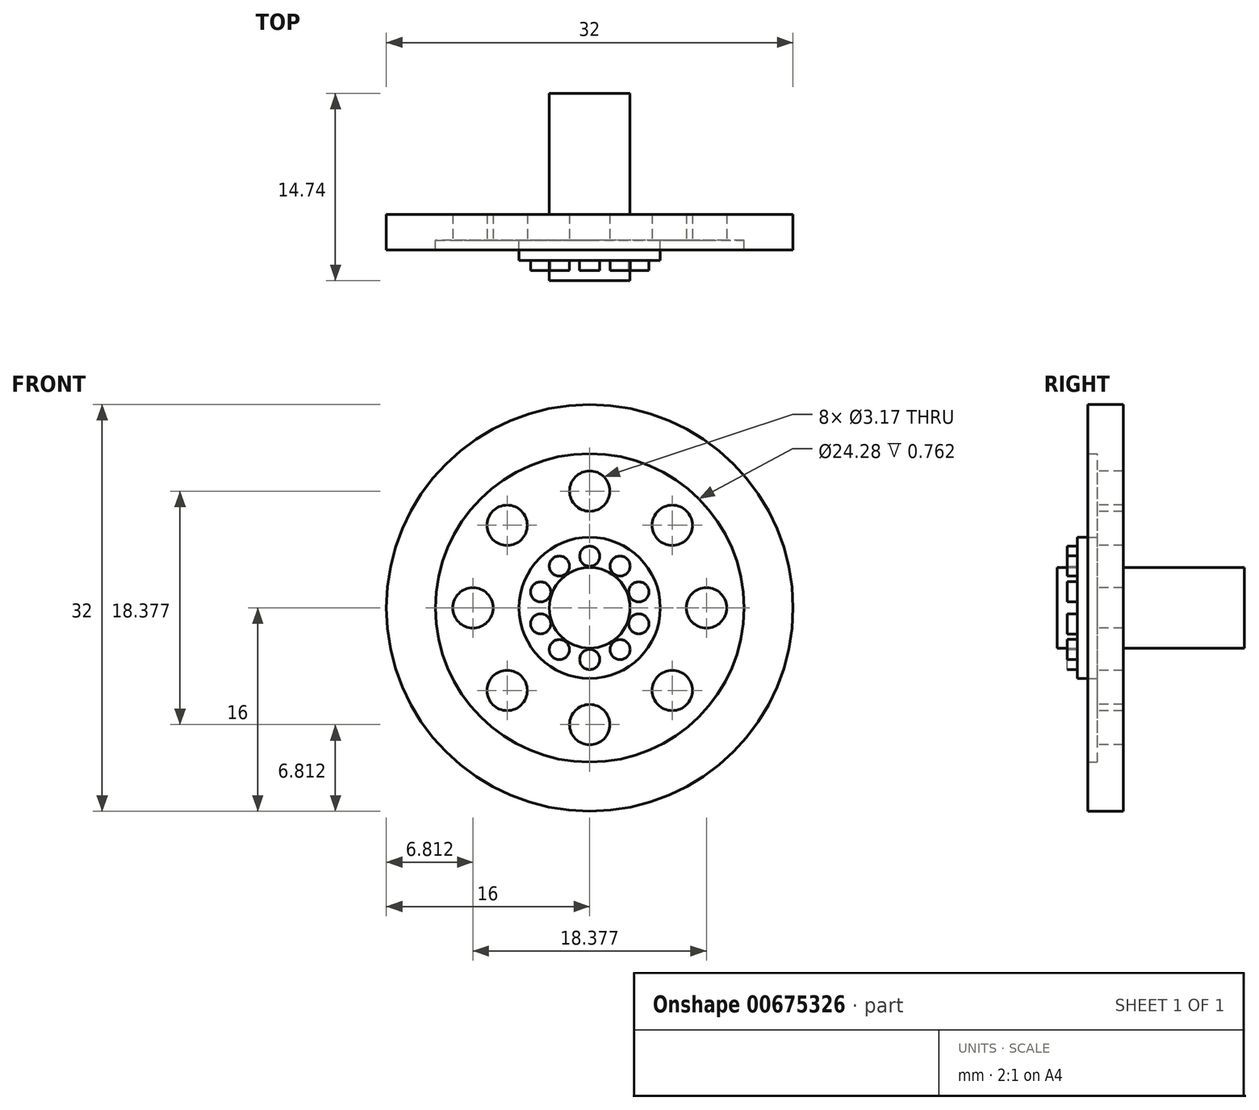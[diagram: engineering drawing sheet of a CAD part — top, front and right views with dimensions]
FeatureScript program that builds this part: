
annotation { "Feature Type Name" : "Feature", "Feature Type Description" : "" }
export const myFeature = defineFeature(function(context is Context, id is Id, definition is map)
    precondition{}
    {
        {
            var Q0;
            Q0=qCreatedBy(makeId("Front.planeOp"),FACE);
            var sketch = newSketch(context, id + "F0", { "sketchPlane" : qUnion([Q0])});
            skCircle(sketch, "E0", {"center": v(0, 0) * mm, "radius": 16 * mm});
            skSolve(sketch);
        }
        {
            var Q0;
            Q0 = qSketchRegion(id + "F0", true);
            extrude(context, id + "F1", {"entities" : qUnion([Q0]), "depth" : 2.03 * mm, "offsetDistance" : 25.4 * mm});
        }
        {
            var Q0;
            Q0=makeQuery(id+"F1.opExtrude","CAP_FACE",FACE,{"disambiguationData":[OSD([sQuery(id+"F0.wireOp",EDGE,"E0")])],"isStart":false});
            var sketch = newSketch(context, id + "F2", { "sketchPlane" : qUnion([Q0])});
            skCircle(sketch, "E1", {"center": v(0, 9.19) * mm, "radius": 1.59 * mm});
            skCircle(sketch, "E2.1.0", {"center": v(-6.5, 6.5) * mm, "radius": 1.59 * mm});
            skCircle(sketch, "E2.2.0", {"center": v(-9.19, 0) * mm, "radius": 1.59 * mm});
            skCircle(sketch, "E2.3.0", {"center": v(-6.5, -6.5) * mm, "radius": 1.59 * mm});
            skCircle(sketch, "E2.4.0", {"center": v(0, -9.19) * mm, "radius": 1.59 * mm});
            skCircle(sketch, "E2.5.0", {"center": v(6.5, -6.5) * mm, "radius": 1.59 * mm});
            skCircle(sketch, "E2.6.0", {"center": v(9.19, 0) * mm, "radius": 1.59 * mm});
            skCircle(sketch, "E2.7.0", {"center": v(6.5, 6.5) * mm, "radius": 1.59 * mm});
            skPoint(sketch, "E2.center", {"position": v(0, 0) * mm});
            skSolve(sketch);
        }
        {
            var Q0;
            Q0=makeQuery(id+"F2.imprint","IMPRINT",FACE,{"disambiguationData":[TD([[makeQuery(id+"F2.imprint","IMPRINT",EDGE,{"derivedFrom":sQuery(id+"F2.wireOp",EDGE,"E1")}),1.0]])]});
            var Q1;
            Q1=makeQuery(id+"F2.imprint","IMPRINT",FACE,{"disambiguationData":[TD([[makeQuery(id+"F2.imprint","IMPRINT",EDGE,{"derivedFrom":sQuery(id+"F2.wireOp",EDGE,"E2.7.0")}),1.0]])]});
            var Q2;
            Q2=makeQuery(id+"F2.imprint","IMPRINT",FACE,{"disambiguationData":[TD([[makeQuery(id+"F2.imprint","IMPRINT",EDGE,{"derivedFrom":sQuery(id+"F2.wireOp",EDGE,"E2.6.0")}),1.0]])]});
            var Q3;
            Q3=makeQuery(id+"F2.imprint","IMPRINT",FACE,{"disambiguationData":[TD([[makeQuery(id+"F2.imprint","IMPRINT",EDGE,{"derivedFrom":sQuery(id+"F2.wireOp",EDGE,"E2.5.0")}),1.0]])]});
            var Q4;
            Q4=makeQuery(id+"F2.imprint","IMPRINT",FACE,{"disambiguationData":[TD([[makeQuery(id+"F2.imprint","IMPRINT",EDGE,{"derivedFrom":sQuery(id+"F2.wireOp",EDGE,"E2.4.0")}),1.0]])]});
            var Q5;
            Q5=makeQuery(id+"F2.imprint","IMPRINT",FACE,{"disambiguationData":[TD([[makeQuery(id+"F2.imprint","IMPRINT",EDGE,{"derivedFrom":sQuery(id+"F2.wireOp",EDGE,"E2.3.0")}),1.0]])]});
            var Q6;
            Q6=makeQuery(id+"F2.imprint","IMPRINT",FACE,{"disambiguationData":[TD([[makeQuery(id+"F2.imprint","IMPRINT",EDGE,{"derivedFrom":sQuery(id+"F2.wireOp",EDGE,"E2.2.0")}),1.0]])]});
            var Q7;
            Q7=makeQuery(id+"F2.imprint","IMPRINT",FACE,{"disambiguationData":[TD([[makeQuery(id+"F2.imprint","IMPRINT",EDGE,{"derivedFrom":sQuery(id+"F2.wireOp",EDGE,"E2.1.0")}),1.0]])]});
            extrude(context, id + "F3", {"entities" : qUnion([Q0, Q1, Q2, Q3, Q4, Q5, Q6, Q7]), "operationType" : NewBodyOperationType.REMOVE, "oppositeDirection" : true, "depth" : 20.32 * mm, "offsetDistance" : 25.4 * mm});
        }
        {
            var Q0;
            Q0=makeQuery(id+"F1.opExtrude","CAP_FACE",FACE,{"disambiguationData":[OSD([sQuery(id+"F0.wireOp",EDGE,"E0")])],"isStart":false});
            var sketch = newSketch(context, id + "F4", { "sketchPlane" : qUnion([Q0])});
            skCircle(sketch, "E3", {"center": v(0, 0) * mm, "radius": 5.56 * mm});
            skSolve(sketch);
        }
        {
            var Q0;
            Q0=makeQuery(id+"F4.imprint","IMPRINT",FACE,{"disambiguationData":[TD([[makeQuery(id+"F4.imprint","IMPRINT",EDGE,{"derivedFrom":sQuery(id+"F4.wireOp",EDGE,"E3")}),1.0]])]});
            var sketch = newSketch(context, id + "F5", { "sketchPlane" : qUnion([Q0])});
            skCircle(sketch, "E4", {"center": v(0, 0) * mm, "radius": 3.17 * mm});
            skSolve(sketch);
        }
        {
            var Q0;
            Q0=makeQuery(id+"F5.imprint","IMPRINT",FACE,{"disambiguationData":[TD([[makeQuery(id+"F5.imprint","IMPRINT",EDGE,{"derivedFrom":sQuery(id+"F5.wireOp",EDGE,"E4")}),1.0]])]});
            extrude(context, id + "F6", {"entities" : qUnion([Q0]), "operationType" : NewBodyOperationType.ADD, "depth" : 3.17 * mm, "offsetDistance" : 25.4 * mm});
        }
        {
            var Q0;
            Q0=makeQuery(id+"F4.imprint","IMPRINT",FACE,{"disambiguationData":[TD([[makeQuery(id+"F4.imprint","IMPRINT",EDGE,{"derivedFrom":sQuery(id+"F4.wireOp",EDGE,"E3")}),1.0]])]});
            extrude(context, id + "F7", {"entities" : qUnion([Q0]), "operationType" : NewBodyOperationType.ADD, "depth" : 1.59 * mm, "offsetDistance" : 25.4 * mm});
        }
        {
            var Q0;
            Q0=makeQuery(id+"F7.opExtrude","CAP_FACE",FACE,{"disambiguationData":[OSD([sQuery(id+"F4.wireOp",EDGE,"E3")])],"isStart":false});
            var sketch = newSketch(context, id + "F8", { "sketchPlane" : qUnion([Q0])});
            skCircle(sketch, "E5", {"center": v(0, 4.06) * mm, "radius": 0.8 * mm});
            skCircle(sketch, "E6.1.0", {"center": v(-2.39, 3.29) * mm, "radius": 0.8 * mm});
            skCircle(sketch, "E6.2.0", {"center": v(-3.86, 1.26) * mm, "radius": 0.8 * mm});
            skCircle(sketch, "E6.3.0", {"center": v(-3.86, -1.26) * mm, "radius": 0.8 * mm});
            skCircle(sketch, "E6.4.0", {"center": v(-2.39, -3.29) * mm, "radius": 0.8 * mm});
            skCircle(sketch, "E6.5.0", {"center": v(0, -4.06) * mm, "radius": 0.8 * mm});
            skCircle(sketch, "E6.6.0", {"center": v(2.39, -3.29) * mm, "radius": 0.8 * mm});
            skCircle(sketch, "E6.7.0", {"center": v(3.86, -1.26) * mm, "radius": 0.8 * mm});
            skCircle(sketch, "E6.8.0", {"center": v(3.86, 1.26) * mm, "radius": 0.8 * mm});
            skCircle(sketch, "E6.9.0", {"center": v(2.39, 3.29) * mm, "radius": 0.8 * mm});
            skPoint(sketch, "E6.center", {"position": v(0, 0) * mm});
            skSolve(sketch);
        }
        {
            var Q0;
            Q0=makeQuery(id+"F8.imprint","IMPRINT",FACE,{"disambiguationData":[TD([[makeQuery(id+"F8.imprint","IMPRINT",EDGE,{"derivedFrom":sQuery(id+"F8.wireOp",EDGE,"E5")}),1.0]])]});
            var Q1;
            Q1=makeQuery(id+"F8.imprint","IMPRINT",FACE,{"disambiguationData":[TD([[makeQuery(id+"F8.imprint","IMPRINT",EDGE,{"derivedFrom":sQuery(id+"F8.wireOp",EDGE,"E6.9.0")}),1.0]])]});
            var Q2;
            Q2=makeQuery(id+"F8.imprint","IMPRINT",FACE,{"disambiguationData":[TD([[makeQuery(id+"F8.imprint","IMPRINT",EDGE,{"derivedFrom":sQuery(id+"F8.wireOp",EDGE,"E6.8.0")}),1.0]])]});
            var Q3;
            Q3=makeQuery(id+"F8.imprint","IMPRINT",FACE,{"disambiguationData":[TD([[makeQuery(id+"F8.imprint","IMPRINT",EDGE,{"derivedFrom":sQuery(id+"F8.wireOp",EDGE,"E6.7.0")}),1.0]])]});
            var Q4;
            Q4=makeQuery(id+"F8.imprint","IMPRINT",FACE,{"disambiguationData":[TD([[makeQuery(id+"F8.imprint","IMPRINT",EDGE,{"derivedFrom":sQuery(id+"F8.wireOp",EDGE,"E6.6.0")}),1.0]])]});
            var Q5;
            Q5=makeQuery(id+"F8.imprint","IMPRINT",FACE,{"disambiguationData":[TD([[makeQuery(id+"F8.imprint","IMPRINT",EDGE,{"derivedFrom":sQuery(id+"F8.wireOp",EDGE,"E6.5.0")}),1.0]])]});
            var Q6;
            Q6=makeQuery(id+"F8.imprint","IMPRINT",FACE,{"disambiguationData":[TD([[makeQuery(id+"F8.imprint","IMPRINT",EDGE,{"derivedFrom":sQuery(id+"F8.wireOp",EDGE,"E6.4.0")}),1.0]])]});
            var Q7;
            Q7=makeQuery(id+"F8.imprint","IMPRINT",FACE,{"disambiguationData":[TD([[makeQuery(id+"F8.imprint","IMPRINT",EDGE,{"derivedFrom":sQuery(id+"F8.wireOp",EDGE,"E6.3.0")}),1.0]])]});
            var Q8;
            Q8=makeQuery(id+"F8.imprint","IMPRINT",FACE,{"disambiguationData":[TD([[makeQuery(id+"F8.imprint","IMPRINT",EDGE,{"derivedFrom":sQuery(id+"F8.wireOp",EDGE,"E6.2.0")}),1.0]])]});
            var Q9;
            Q9=makeQuery(id+"F8.imprint","IMPRINT",FACE,{"disambiguationData":[TD([[makeQuery(id+"F8.imprint","IMPRINT",EDGE,{"derivedFrom":sQuery(id+"F8.wireOp",EDGE,"E6.1.0")}),1.0]])]});
            extrude(context, id + "F9", {"entities" : qUnion([Q0, Q1, Q2, Q3, Q4, Q5, Q6, Q7, Q8, Q9]), "depth" : 0.8 * mm, "offsetDistance" : 25.4 * mm});
        }
        {
            var Q0;
            Q0=makeQuery(id+"F1.opExtrude","CAP_FACE",FACE,{"disambiguationData":[OSD([sQuery(id+"F0.wireOp",EDGE,"E0")])],"isStart":true});
            var sketch = newSketch(context, id + "F10", { "sketchPlane" : qUnion([Q0])});
            skCircle(sketch, "E7", {"center": v(0, 0) * mm, "radius": 3.18 * mm});
            skSolve(sketch);
        }
        {
            var Q0;
            Q0=makeQuery(id+"F10.imprint","IMPRINT",FACE,{"disambiguationData":[TD([[makeQuery(id+"F10.imprint","IMPRINT",EDGE,{"derivedFrom":sQuery(id+"F10.wireOp",EDGE,"E7")}),1.0]])]});
            extrude(context, id + "F11", {"entities" : qUnion([Q0]), "operationType" : NewBodyOperationType.ADD, "depth" : 9.52 * mm, "offsetDistance" : 25.4 * mm});
        }
        {
            var Q0;
            Q0=makeQuery(id+"F1.opExtrude","CAP_FACE",FACE,{"disambiguationData":[OSD([sQuery(id+"F0.wireOp",EDGE,"E0")])],"isStart":false});
            var sketch = newSketch(context, id + "F12", { "sketchPlane" : qUnion([Q0])});
            skCircle(sketch, "E8", {"center": v(0, 0) * mm, "radius": 12.14 * mm});
            skSolve(sketch);
        }
        {
            var Q0;
            Q0=makeQuery(id+"F12.imprint","IMPRINT",FACE,{"disambiguationData":[TD([[makeQuery(id+"F12.imprint","IMPRINT",EDGE,{"derivedFrom":sQuery(id+"F12.wireOp",EDGE,"E8")}),-1.0]])]});
            extrude(context, id + "F13", {"entities" : qUnion([Q0]), "operationType" : NewBodyOperationType.ADD, "depth" : 0.76 * mm, "offsetDistance" : 25.4 * mm});
        }
    });
